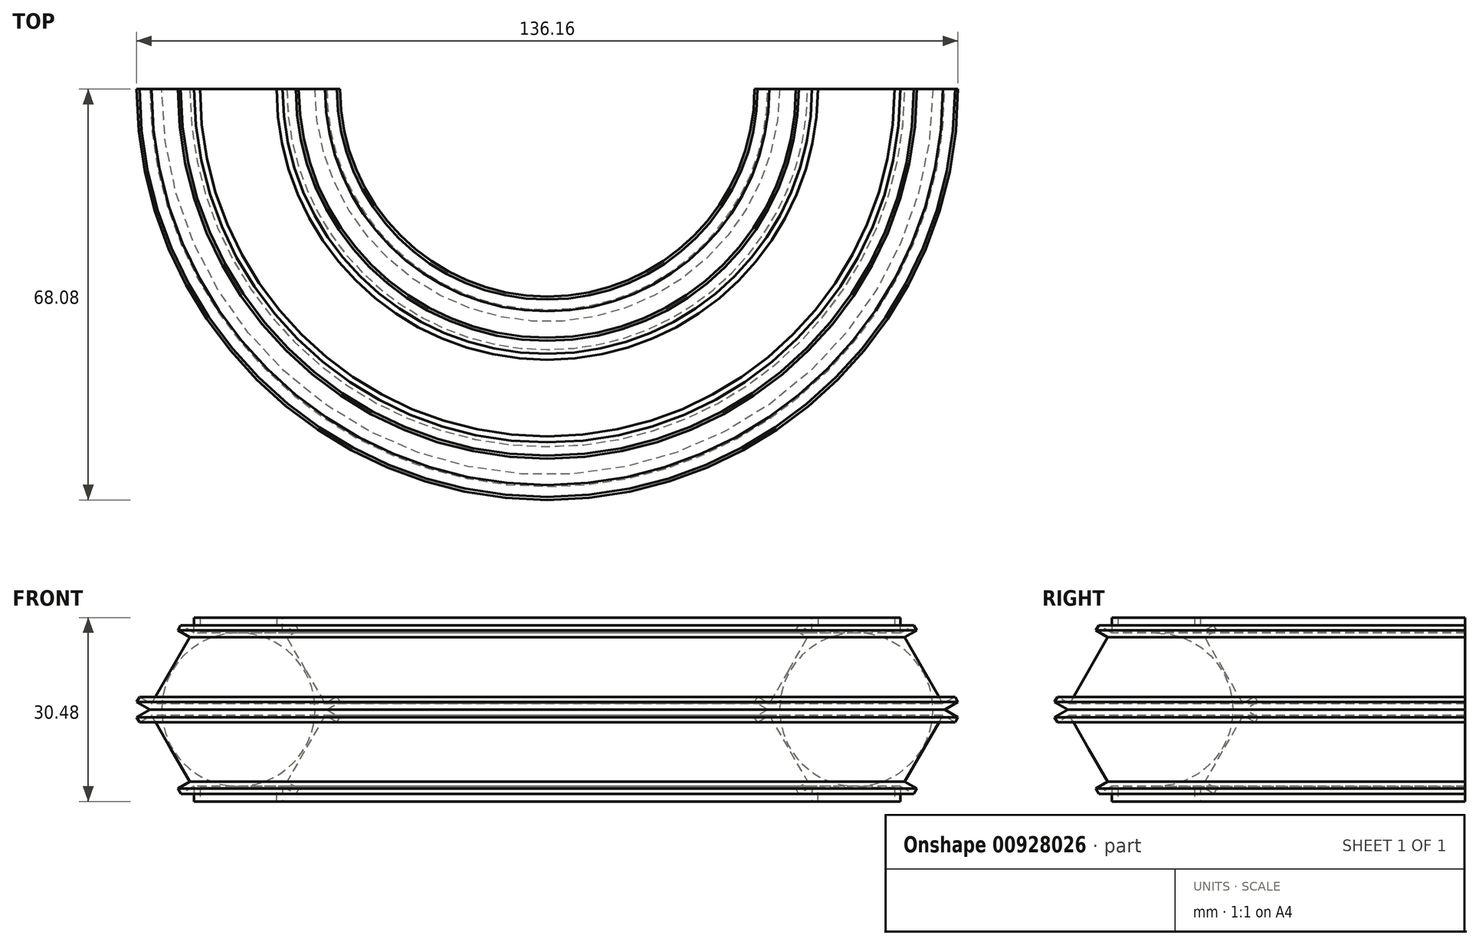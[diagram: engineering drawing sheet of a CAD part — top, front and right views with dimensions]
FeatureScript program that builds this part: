
annotation { "Feature Type Name" : "Feature", "Feature Type Description" : "" }
export const myFeature = defineFeature(function(context is Context, id is Id, definition is map)
    precondition{}
    {
        {
            var Q0;
            Q0=qCreatedBy(makeId("Top.planeOp"),FACE);
            var sketch = newSketch(context, id + "F0", { "sketchPlane" : qUnion([Q0])});
            skLineSegment(sketch, "E0", {"start": v(0, 0) * mm, "end": v(-50.8, 0) * mm});
            skCircle(sketch, "E1", {"center": v(0, 0) * mm, "radius": 50.8 * mm});
            skSolve(sketch);
        }
        {
            var Q0;
            Q0=qCreatedBy(makeId("Front.planeOp"),FACE);
            var sketch = newSketch(context, id + "F1", { "sketchPlane" : qUnion([Q0])});
            skCircle(sketch, "E2", {"center": v(-51.22, 0) * mm, "radius": 12.7 * mm});
            skPoint(sketch, "E3.0.midPoint", {"position": v(-51.22, 12.7) * mm});
            skLineSegment(sketch, "E4", {"start": v(-65.88, 0) * mm, "end": v(-68.08, -1.27) * mm});
            skLineSegment(sketch, "E5", {"start": v(-58.55, -12.7) * mm, "end": v(-60.75, -13.97) * mm});
            skLineSegment(sketch, "E6", {"start": v(-58.55, -12.7) * mm, "end": v(-58.55, -15.23) * mm});
            skLineSegment(sketch, "E7", {"start": v(-43.88, -12.7) * mm, "end": v(-43.88, -15.23) * mm});
            skLineSegment(sketch, "E8", {"start": v(-43.88, -12.7) * mm, "end": v(-41.67, -13.98) * mm});
            skLineSegment(sketch, "E9", {"start": v(-36.55, 0) * mm, "end": v(-34.36, -1.26) * mm});
            skLineSegment(sketch, "E10", {"start": v(-36.55, 0) * mm, "end": v(-34.36, 1.26) * mm});
            skLineSegment(sketch, "E11", {"start": v(-43.88, 12.7) * mm, "end": v(-41.7, 13.97) * mm});
            skLineSegment(sketch, "E12", {"start": v(-58.55, 12.7) * mm, "end": v(-58.55, 15.25) * mm});
            skLineSegment(sketch, "E13", {"start": v(-43.88, 12.7) * mm, "end": v(-43.88, 15.25) * mm});
            skLineSegment(sketch, "E14", {"start": v(-58.55, 12.7) * mm, "end": v(-60.76, 13.98) * mm});
            skLineSegment(sketch, "E15", {"start": v(-65.88, 0) * mm, "end": v(-68.08, 1.27) * mm});
            skLineSegment(sketch, "E16", {"start": v(-44.86, 15.25) * mm, "end": v(-43.88, 15.25) * mm});
            skLineSegment(sketch, "E17", {"start": v(-57.56, 15.25) * mm, "end": v(-58.55, 15.25) * mm});
            skLineSegment(sketch, "E18", {"start": v(-51.22, 12.96) * mm, "end": v(-57.56, 12.96) * mm});
            skLineSegment(sketch, "E19", {"start": v(-51.22, 12.96) * mm, "end": v(-44.86, 12.96) * mm});
            skLineSegment(sketch, "E20", {"start": v(-61.25, 13.12) * mm, "end": v(-60.76, 13.98) * mm});
            skLineSegment(sketch, "E21", {"start": v(-67.6, 2.11) * mm, "end": v(-68.08, 1.27) * mm});
            skLineSegment(sketch, "E22", {"start": v(-62.43, 6.47) * mm, "end": v(-59.25, 11.97) * mm});
            skLineSegment(sketch, "E23", {"start": v(-61.24, -13.11) * mm, "end": v(-60.75, -13.97) * mm});
            skLineSegment(sketch, "E24", {"start": v(-67.6, -2.12) * mm, "end": v(-68.08, -1.27) * mm});
            skLineSegment(sketch, "E25", {"start": v(-62.43, -6.47) * mm, "end": v(-65.6, -0.98) * mm});
            skLineSegment(sketch, "E26", {"start": v(-62.43, -6.47) * mm, "end": v(-59.26, -11.97) * mm});
            skLineSegment(sketch, "E27", {"start": v(-57.56, -15.23) * mm, "end": v(-58.55, -15.23) * mm});
            skLineSegment(sketch, "E28", {"start": v(-44.86, -15.23) * mm, "end": v(-43.88, -15.23) * mm});
            skLineSegment(sketch, "E29", {"start": v(-51.22, -12.95) * mm, "end": v(-57.56, -12.95) * mm});
            skLineSegment(sketch, "E30", {"start": v(-51.22, -12.95) * mm, "end": v(-44.86, -12.95) * mm});
            skLineSegment(sketch, "E31", {"start": v(-41.18, -13.12) * mm, "end": v(-41.67, -13.98) * mm});
            skLineSegment(sketch, "E32", {"start": v(-34.85, -2.11) * mm, "end": v(-34.36, -1.26) * mm});
            skLineSegment(sketch, "E33", {"start": v(-40, -6.48) * mm, "end": v(-36.83, -0.97) * mm});
            skLineSegment(sketch, "E34", {"start": v(-40, -6.48) * mm, "end": v(-43.16, -11.98) * mm});
            skLineSegment(sketch, "E35", {"start": v(-34.86, 2.13) * mm, "end": v(-34.36, 1.26) * mm});
            skLineSegment(sketch, "E36", {"start": v(-41.2, 13.11) * mm, "end": v(-41.7, 13.97) * mm});
            skLineSegment(sketch, "E37", {"start": v(-40, 6.48) * mm, "end": v(-43.17, 11.98) * mm});
            skLineSegment(sketch, "E38", {"start": v(-40, 6.48) * mm, "end": v(-36.83, 1) * mm});
            skLineSegment(sketch, "E39", {"start": v(-62.43, 6.47) * mm, "end": v(-65.6, 0.96) * mm});
            skLineSegment(sketch, "E40", {"start": v(-61.25, 13.12) * mm, "end": v(-59.25, 11.97) * mm});
            skLineSegment(sketch, "E41", {"start": v(-57.56, 15.25) * mm, "end": v(-57.56, 12.96) * mm});
            skLineSegment(sketch, "E42", {"start": v(-67.6, -2.12) * mm, "end": v(-65.6, -0.98) * mm});
            skLineSegment(sketch, "E43", {"start": v(-44.86, -15.23) * mm, "end": v(-44.86, -12.95) * mm});
            skLineSegment(sketch, "E44", {"start": v(-57.56, -12.95) * mm, "end": v(-57.56, -15.23) * mm});
            skLineSegment(sketch, "E45", {"start": v(-41.18, -13.12) * mm, "end": v(-43.16, -11.98) * mm});
            skLineSegment(sketch, "E46", {"start": v(-34.85, -2.11) * mm, "end": v(-36.83, -0.97) * mm});
            skLineSegment(sketch, "E47", {"start": v(-34.86, 2.13) * mm, "end": v(-36.83, 1) * mm});
            skLineSegment(sketch, "E48", {"start": v(-41.2, 13.11) * mm, "end": v(-43.17, 11.98) * mm});
            skLineSegment(sketch, "E49", {"start": v(-44.86, 15.25) * mm, "end": v(-44.86, 12.96) * mm});
            skLineSegment(sketch, "E50", {"start": v(-61.24, -13.11) * mm, "end": v(-59.26, -11.97) * mm});
            skLineSegment(sketch, "E51", {"start": v(-67.6, 2.11) * mm, "end": v(-65.6, 0.96) * mm});
            skLineSegment(sketch, "E52", {"start": v(-51.22, 12.7) * mm, "end": v(-51.22, 0) * mm});
            skSolve(sketch);
        }
        {
            var Q0;
            Q0=makeQuery(id+"F1.imprint","IMPRINT",FACE,{"disambiguationData":[TD([[makeQuery(id+"F1.imprint","IMPRINT",EDGE,{"derivedFrom":sQuery(id+"F1.wireOp",EDGE,"E2")}),-1.0]])]});
            var Q1;
            Q1=sQuery(id+"F0.wireOp",EDGE,"E1");
            revolve(context, id + "F2", {"surfaceOperationType" : NewSurfaceOperationType.NEW, "entities" : qUnion([Q0]), "axis" : qUnion([Q1]), "revolveType" : RevolveType.ONE_DIRECTION, "angle" : 180 * degree});
        }
    });
